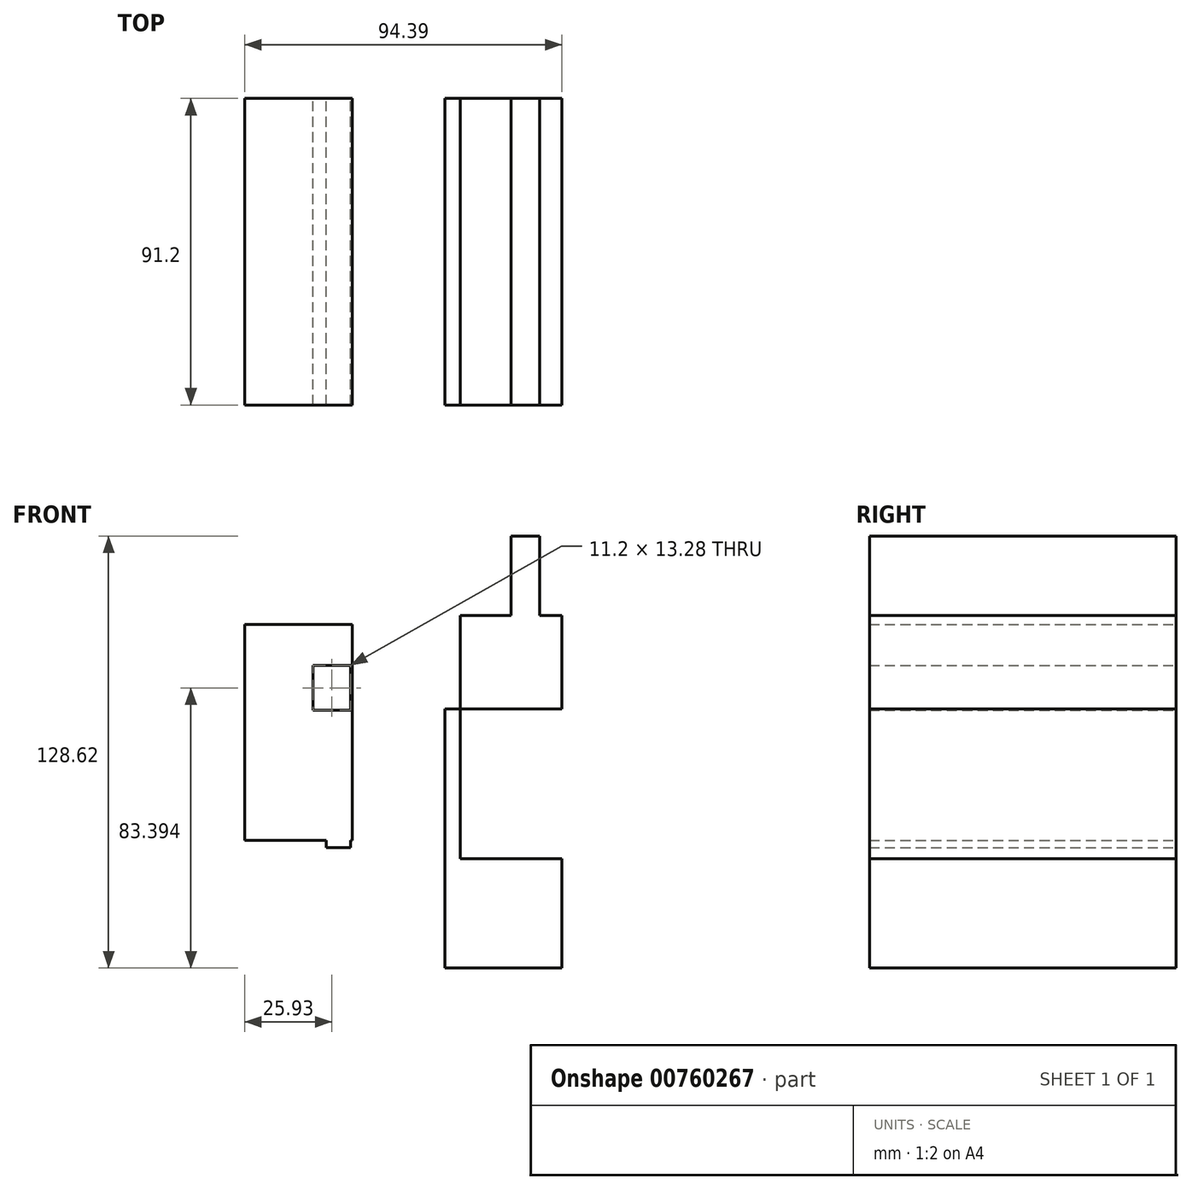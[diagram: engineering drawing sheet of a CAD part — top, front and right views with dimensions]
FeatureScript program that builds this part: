
annotation { "Feature Type Name" : "Feature", "Feature Type Description" : "" }
export const myFeature = defineFeature(function(context is Context, id is Id, definition is map)
    precondition{}
    {
        {
            var Q0;
            Q0=qCreatedBy(makeId("Front.planeOp"),FACE);
            var sketch = newSketch(context, id + "F0", { "sketchPlane" : qUnion([Q0])});
            skLineSegment(sketch, "E0.bottom", {"start": v(-29.25, 37.34) * mm, "end": v(-18.05, 37.34) * mm});
            skLineSegment(sketch, "E0.top", {"start": v(-29.25, 24.07) * mm, "end": v(-18.05, 24.07) * mm});
            skLineSegment(sketch, "E0.left", {"start": v(-29.25, 37.34) * mm, "end": v(-29.25, 24.07) * mm});
            skLineSegment(sketch, "E0.right", {"start": v(-18.05, 37.34) * mm, "end": v(-18.05, 24.07) * mm});
            skLineSegment(sketch, "E1.bottom", {"start": v(-25.3, 12.03) * mm, "end": v(-18.05, 12.03) * mm});
            skLineSegment(sketch, "E1.top", {"start": v(-25.3, -16.8) * mm, "end": v(-18.05, -16.8) * mm});
            skLineSegment(sketch, "E1.left", {"start": v(-25.3, 12.03) * mm, "end": v(-25.3, -16.8) * mm});
            skLineSegment(sketch, "E1.right", {"start": v(-18.05, 12.03) * mm, "end": v(-18.05, -16.8) * mm});
            skLineSegment(sketch, "E2.bottom", {"start": v(44.81, -20.12) * mm, "end": v(14.52, -20.12) * mm});
            skLineSegment(sketch, "E2.top", {"start": v(44.81, 52.28) * mm, "end": v(14.52, 52.28) * mm});
            skLineSegment(sketch, "E2.left", {"start": v(44.81, -20.12) * mm, "end": v(44.81, 52.28) * mm});
            skLineSegment(sketch, "E2.right", {"start": v(14.52, -20.12) * mm, "end": v(14.52, 52.28) * mm});
            skLineSegment(sketch, "E3.bottom", {"start": v(-17.63, 49.58) * mm, "end": v(-49.58, 49.58) * mm});
            skLineSegment(sketch, "E3.top", {"start": v(-17.63, -14.73) * mm, "end": v(-49.58, -14.73) * mm});
            skLineSegment(sketch, "E3.left", {"start": v(-17.63, 49.58) * mm, "end": v(-17.63, -14.73) * mm});
            skLineSegment(sketch, "E3.right", {"start": v(-49.58, 49.58) * mm, "end": v(-49.58, -14.73) * mm});
            skLineSegment(sketch, "E4.bottom", {"start": v(9.96, -52.7) * mm, "end": v(44.81, -52.7) * mm});
            skLineSegment(sketch, "E4.top", {"start": v(9.96, 24.48) * mm, "end": v(44.81, 24.48) * mm});
            skLineSegment(sketch, "E4.left", {"start": v(9.96, -52.7) * mm, "end": v(9.96, 24.48) * mm});
            skLineSegment(sketch, "E4.right", {"start": v(44.81, -52.7) * mm, "end": v(44.81, 24.48) * mm});
            skLineSegment(sketch, "E5.bottom", {"start": v(38.17, 75.93) * mm, "end": v(29.67, 75.93) * mm});
            skLineSegment(sketch, "E5.top", {"start": v(38.17, 52.28) * mm, "end": v(29.67, 52.28) * mm});
            skLineSegment(sketch, "E5.left", {"start": v(38.17, 75.93) * mm, "end": v(38.17, 52.28) * mm});
            skLineSegment(sketch, "E5.right", {"start": v(29.67, 75.93) * mm, "end": v(29.67, 52.28) * mm});
            skSolve(sketch);
        }
        {
            var Q0;
            Q0=makeQuery(id+"F0.imprint","IMPRINT",FACE,{"disambiguationData":[TD([[makeQuery(id+"F0.imprint","IMPRINT",EDGE,{"derivedFrom":sQuery(id+"F0.wireOp",EDGE,"E5.bottom")}),1.0]])]});
            var Q1;
            Q1=makeQuery(id+"F0.imprint","IMPRINT",FACE,{"disambiguationData":[TD([[makeQuery(id+"F0.imprint","IMPRINT",EDGE,{"derivedFrom":sQuery(id+"F0.wireOp",EDGE,"E0.bottom")}),1.0]])]});
            var Q2;
            {var subQ0=sQuery(id+"F0.wireOp",EDGE,"E1.top");Q2=makeQuery(id+"F0.imprint","IMPRINT",FACE,{"disambiguationData":[TD([[makeQuery(id+"F0.imprint","IMPRINT",EDGE,{"derivedFrom":subQ0}),1.0]])]});}
            var Q3;
            {var subQ0=sQuery(id+"F0.wireOp",EDGE,"E1.bottom");Q3=makeQuery(id+"F0.imprint","IMPRINT",FACE,{"disambiguationData":[TD([[makeQuery(id+"F0.imprint","IMPRINT",EDGE,{"derivedFrom":subQ0}),-1.0]])]});}
            var Q4;
            {var subQ4=sQuery(id+"F0.wireOp",EDGE,"E2.bottom");Q4=makeQuery(id+"F0.imprint","IMPRINT",FACE,{"disambiguationData":[TD([[makeQuery(id+"F0.imprint","IMPRINT",EDGE,{"derivedFrom":subQ4}),1.0]])]});}
            var Q5;
            {var subQ1=sQuery(id+"F0.wireOp",EDGE,"E2.top");var subQ6=makeQuery(id+"F0.imprint","INTERSECT",VERTEX,{"derivedFrom":[subQ1,sQuery(id+"F0.wireOp",EDGE,"E5.right")]});Q5=makeQuery(id+"F0.imprint","IMPRINT",FACE,{"disambiguationData":[TD([[makeQuery(id+"F0.imprint","IMPRINT",EDGE,{"disambiguationData":[TD([[subQ6,-1.0]])],"derivedFrom":subQ1}),1.0]])]});}
            extrude(context, id + "F1", {"entities" : qUnion([Q0, Q1, Q2, Q3, Q4, Q5]), "depth" : 91.2 * mm, "offsetDistance" : 25.4 * mm});
        }
    });
